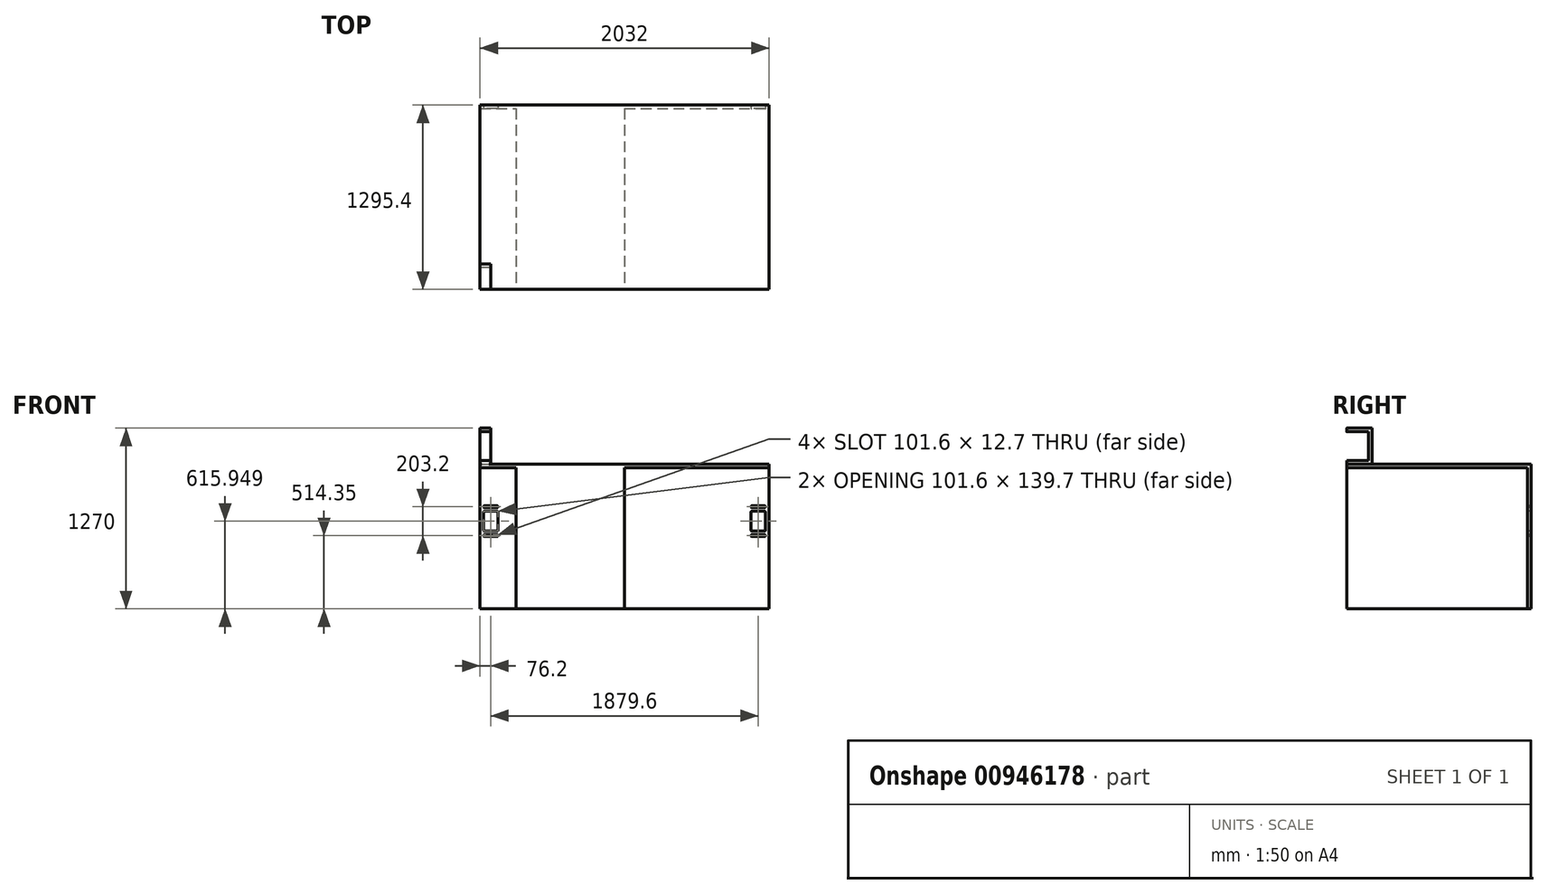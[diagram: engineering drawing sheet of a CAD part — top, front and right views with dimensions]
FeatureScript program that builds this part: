
annotation { "Feature Type Name" : "Feature", "Feature Type Description" : "" }
export const myFeature = defineFeature(function(context is Context, id is Id, definition is map)
    precondition{}
    {
        {
            var Q0;
            Q0=qCreatedBy(makeId("Front.planeOp"),FACE);
            var sketch = newSketch(context, id + "F0", { "sketchPlane" : qUnion([Q0])});
            skLineSegment(sketch, "E0.bottom", {"start": v(-762, 1162) * mm, "end": v(0, 1162) * mm});
            skLineSegment(sketch, "E0.top", {"start": v(-762, 146) * mm, "end": v(0, 146) * mm});
            skLineSegment(sketch, "E0.left", {"start": v(-762, 1162) * mm, "end": v(-762, 146) * mm});
            skLineSegment(sketch, "E0.right", {"start": v(0, 1162) * mm, "end": v(0, 146) * mm});
            skSolve(sketch);
        }
        {
            var Q0;
            Q0=qSketchRegion(id+"F0",true);
            extrude(context, id + "F1", {"entities" : qUnion([Q0]), "depth" : 1270 * mm, "offsetDistance" : 25.4 * mm});
        }
        {
            var Q0;
            Q0=makeQuery(id+"F1.opExtrude","CAP_FACE",FACE,{"disambiguationData":[OSD([sQuery(id+"F0.wireOp",EDGE,"E0.bottom"),sQuery(id+"F0.wireOp",EDGE,"E0.top"),sQuery(id+"F0.wireOp",EDGE,"E0.left"),sQuery(id+"F0.wireOp",EDGE,"E0.right")])],"isStart":true});
            var sketch = newSketch(context, id + "F2", { "sketchPlane" : qUnion([Q0])});
            skLineSegment(sketch, "E1.bottom", {"start": v(1016, 1162) * mm, "end": v(-1016, 1162) * mm});
            skLineSegment(sketch, "E1.top", {"start": v(1016, 146) * mm, "end": v(-1016, 146) * mm});
            skLineSegment(sketch, "E1.left", {"start": v(1016, 1162) * mm, "end": v(1016, 146) * mm});
            skLineSegment(sketch, "E1.right", {"start": v(-1016, 1162) * mm, "end": v(-1016, 146) * mm});
            skSolve(sketch);
        }
        {
            var Q0;
            Q0=qSketchRegion(id+"F2",true);
            extrude(context, id + "F3", {"entities" : qUnion([Q0]), "operationType" : NewBodyOperationType.ADD, "depth" : 25.4 * mm, "offsetDistance" : 25.4 * mm});
        }
        {
            var Q0;
            {var subQ0=sQuery(id+"F2.wireOp",EDGE,"E1.top");var subQ1=sQuery(id+"F2.wireOp",EDGE,"E1.bottom");var subQ2=sQuery(id+"F2.wireOp",EDGE,"E1.left");Q0=makeQuery(id+"F3.boolean.opBoolean","SPLIT",FACE,{"disambiguationData":[TD([makeQuery(id+"F1.opExtrude","SWEPT_FACE",FACE,{"disambiguationData":[OSD([sQuery(id+"F0.wireOp",EDGE,"E0.left")])]})])],"derivedFrom":makeQuery(id+"F3.opExtrude","CAP_FACE",FACE,{"disambiguationData":[OSD([subQ1,subQ0,subQ2,sQuery(id+"F2.wireOp",EDGE,"E1.right")])],"isStart":true})});}
            var sketch = newSketch(context, id + "F4", { "sketchPlane" : qUnion([Q0])});
            skLineSegment(sketch, "E2.bottom", {"start": v(990.6, 825.45) * mm, "end": v(990.6, 698.45) * mm});
            skLineSegment(sketch, "E2.top", {"start": v(889, 825.45) * mm, "end": v(889, 698.45) * mm});
            skLineSegment(sketch, "E2.left", {"start": v(984.25, 831.8) * mm, "end": v(895.35, 831.8) * mm});
            skLineSegment(sketch, "E2.right", {"start": v(984.25, 692.1) * mm, "end": v(895.35, 692.1) * mm});
            skLineSegment(sketch, "E3.bottom", {"start": v(990.6, 863.55) * mm, "end": v(990.6, 863.55) * mm});
            skLineSegment(sketch, "E3.top", {"start": v(889, 863.55) * mm, "end": v(889, 863.55) * mm});
            skLineSegment(sketch, "E3.left", {"start": v(984.25, 869.9) * mm, "end": v(895.35, 869.9) * mm});
            skLineSegment(sketch, "E3.right", {"start": v(984.25, 857.2) * mm, "end": v(895.35, 857.2) * mm});
            skLineSegment(sketch, "E4.bottom", {"start": v(990.6, 660.35) * mm, "end": v(990.6, 660.35) * mm});
            skLineSegment(sketch, "E4.top", {"start": v(889, 660.35) * mm, "end": v(889, 660.35) * mm});
            skLineSegment(sketch, "E4.left", {"start": v(984.25, 666.7) * mm, "end": v(895.35, 666.7) * mm});
            skLineSegment(sketch, "E4.right", {"start": v(984.25, 654) * mm, "end": v(895.35, 654) * mm});
            skPoint(sketch, "E5.visualSharp", {"position": v(990.6, 869.9) * mm});
            skArc(sketch, "E5.filletArc", {"start": v(990.6, 863.55) * mm, "mid": v(988.74, 868.04) * mm, "end": v(984.25, 869.9) * mm});
            skPoint(sketch, "E6.visualSharp", {"position": v(889, 857.2) * mm});
            skArc(sketch, "E6.filletArc", {"start": v(889, 863.55) * mm, "mid": v(890.86, 859.06) * mm, "end": v(895.35, 857.2) * mm});
            skPoint(sketch, "E7.visualSharp", {"position": v(889, 869.9) * mm});
            skArc(sketch, "E7.filletArc", {"start": v(895.35, 869.9) * mm, "mid": v(890.86, 868.04) * mm, "end": v(889, 863.55) * mm});
            skPoint(sketch, "E8.visualSharp", {"position": v(990.6, 857.2) * mm});
            skArc(sketch, "E8.filletArc", {"start": v(984.25, 857.2) * mm, "mid": v(988.74, 859.06) * mm, "end": v(990.6, 863.55) * mm});
            skPoint(sketch, "E9.visualSharp", {"position": v(990.6, 831.8) * mm});
            skArc(sketch, "E9.filletArc", {"start": v(990.6, 825.45) * mm, "mid": v(988.74, 829.94) * mm, "end": v(984.25, 831.8) * mm});
            skPoint(sketch, "E10.visualSharp", {"position": v(889, 831.8) * mm});
            skArc(sketch, "E10.filletArc", {"start": v(895.35, 831.8) * mm, "mid": v(890.86, 829.94) * mm, "end": v(889, 825.45) * mm});
            skPoint(sketch, "E11.visualSharp", {"position": v(990.6, 692.1) * mm});
            skArc(sketch, "E11.filletArc", {"start": v(984.25, 692.1) * mm, "mid": v(988.74, 693.96) * mm, "end": v(990.6, 698.45) * mm});
            skPoint(sketch, "E12.visualSharp", {"position": v(889, 692.1) * mm});
            skArc(sketch, "E12.filletArc", {"start": v(889, 698.45) * mm, "mid": v(890.86, 693.96) * mm, "end": v(895.35, 692.1) * mm});
            skPoint(sketch, "E13.visualSharp", {"position": v(990.6, 666.7) * mm});
            skArc(sketch, "E13.filletArc", {"start": v(990.6, 660.35) * mm, "mid": v(988.74, 664.84) * mm, "end": v(984.25, 666.7) * mm});
            skPoint(sketch, "E14.visualSharp", {"position": v(889, 654) * mm});
            skArc(sketch, "E14.filletArc", {"start": v(889, 660.35) * mm, "mid": v(890.86, 655.86) * mm, "end": v(895.35, 654) * mm});
            skPoint(sketch, "E15.visualSharp", {"position": v(889, 666.7) * mm});
            skArc(sketch, "E15.filletArc", {"start": v(895.35, 666.7) * mm, "mid": v(890.86, 664.84) * mm, "end": v(889, 660.35) * mm});
            skPoint(sketch, "E16.visualSharp", {"position": v(990.6, 654) * mm});
            skArc(sketch, "E16.filletArc", {"start": v(984.25, 654) * mm, "mid": v(988.74, 655.86) * mm, "end": v(990.6, 660.35) * mm});
            skLineSegment(sketch, "E17.bottom", {"start": v(-889, 825.45) * mm, "end": v(-889, 698.45) * mm});
            skLineSegment(sketch, "E17.top", {"start": v(-990.6, 825.45) * mm, "end": v(-990.6, 698.45) * mm});
            skLineSegment(sketch, "E17.left", {"start": v(-895.35, 831.8) * mm, "end": v(-984.25, 831.8) * mm});
            skLineSegment(sketch, "E17.right", {"start": v(-895.35, 692.1) * mm, "end": v(-984.25, 692.1) * mm});
            skLineSegment(sketch, "E18.bottom", {"start": v(-889, 863.55) * mm, "end": v(-889, 863.55) * mm});
            skLineSegment(sketch, "E18.top", {"start": v(-990.6, 863.55) * mm, "end": v(-990.6, 863.55) * mm});
            skLineSegment(sketch, "E18.left", {"start": v(-895.35, 869.9) * mm, "end": v(-984.25, 869.9) * mm});
            skLineSegment(sketch, "E18.right", {"start": v(-895.35, 857.2) * mm, "end": v(-984.25, 857.2) * mm});
            skLineSegment(sketch, "E19.bottom", {"start": v(-889, 660.35) * mm, "end": v(-889, 660.35) * mm});
            skLineSegment(sketch, "E19.top", {"start": v(-990.6, 660.35) * mm, "end": v(-990.6, 660.35) * mm});
            skLineSegment(sketch, "E19.left", {"start": v(-895.35, 666.7) * mm, "end": v(-984.25, 666.7) * mm});
            skLineSegment(sketch, "E19.right", {"start": v(-895.35, 654) * mm, "end": v(-984.25, 654) * mm});
            skPoint(sketch, "E20.visualSharp", {"position": v(-889, 869.9) * mm});
            skArc(sketch, "E20.filletArc", {"start": v(-889, 863.55) * mm, "mid": v(-890.86, 868.04) * mm, "end": v(-895.35, 869.9) * mm});
            skPoint(sketch, "E21.visualSharp", {"position": v(-990.6, 857.2) * mm});
            skArc(sketch, "E21.filletArc", {"start": v(-990.6, 863.55) * mm, "mid": v(-988.74, 859.06) * mm, "end": v(-984.25, 857.2) * mm});
            skPoint(sketch, "E22.visualSharp", {"position": v(-990.6, 869.9) * mm});
            skArc(sketch, "E22.filletArc", {"start": v(-984.25, 869.9) * mm, "mid": v(-988.74, 868.04) * mm, "end": v(-990.6, 863.55) * mm});
            skPoint(sketch, "E23.visualSharp", {"position": v(-889, 857.2) * mm});
            skArc(sketch, "E23.filletArc", {"start": v(-895.35, 857.2) * mm, "mid": v(-890.86, 859.06) * mm, "end": v(-889, 863.55) * mm});
            skPoint(sketch, "E24.visualSharp", {"position": v(-889, 831.8) * mm});
            skArc(sketch, "E24.filletArc", {"start": v(-889, 825.45) * mm, "mid": v(-890.86, 829.94) * mm, "end": v(-895.35, 831.8) * mm});
            skPoint(sketch, "E25.visualSharp", {"position": v(-990.6, 831.8) * mm});
            skArc(sketch, "E25.filletArc", {"start": v(-984.25, 831.8) * mm, "mid": v(-988.74, 829.94) * mm, "end": v(-990.6, 825.45) * mm});
            skPoint(sketch, "E26.visualSharp", {"position": v(-889, 692.1) * mm});
            skArc(sketch, "E26.filletArc", {"start": v(-895.35, 692.1) * mm, "mid": v(-890.86, 693.96) * mm, "end": v(-889, 698.45) * mm});
            skPoint(sketch, "E27.visualSharp", {"position": v(-990.6, 692.1) * mm});
            skArc(sketch, "E27.filletArc", {"start": v(-990.6, 698.45) * mm, "mid": v(-988.74, 693.96) * mm, "end": v(-984.25, 692.1) * mm});
            skPoint(sketch, "E28.visualSharp", {"position": v(-889, 666.7) * mm});
            skArc(sketch, "E28.filletArc", {"start": v(-889, 660.35) * mm, "mid": v(-890.86, 664.84) * mm, "end": v(-895.35, 666.7) * mm});
            skPoint(sketch, "E29.visualSharp", {"position": v(-990.6, 654) * mm});
            skArc(sketch, "E29.filletArc", {"start": v(-990.6, 660.35) * mm, "mid": v(-988.74, 655.86) * mm, "end": v(-984.25, 654) * mm});
            skPoint(sketch, "E30.visualSharp", {"position": v(-990.6, 666.7) * mm});
            skArc(sketch, "E30.filletArc", {"start": v(-984.25, 666.7) * mm, "mid": v(-988.74, 664.84) * mm, "end": v(-990.6, 660.35) * mm});
            skPoint(sketch, "E31.visualSharp", {"position": v(-889, 654) * mm});
            skArc(sketch, "E31.filletArc", {"start": v(-895.35, 654) * mm, "mid": v(-890.86, 655.86) * mm, "end": v(-889, 660.35) * mm});
            skSolve(sketch);
        }
        {
            var Q0;
            Q0=qSketchRegion(id+"F4",true);
            extrude(context, id + "F5", {"entities" : qUnion([Q0]), "operationType" : NewBodyOperationType.REMOVE, "oppositeDirection" : true, "depth" : 25.4 * mm, "offsetDistance" : 25.4 * mm});
        }
        {
            var Q0;
            Q0=makeQuery(id+"F3.boolean.opBoolean","MERGE",FACE,{"derivedFrom":[makeQuery(id+"F1.opExtrude","SWEPT_FACE",FACE,{"disambiguationData":[OSD([sQuery(id+"F0.wireOp",EDGE,"E0.bottom")])]}),makeQuery(id+"F3.opExtrude","SWEPT_FACE",FACE,{"disambiguationData":[OSD([sQuery(id+"F2.wireOp",EDGE,"E1.bottom")])]})]});
            var sketch = newSketch(context, id + "F6", { "sketchPlane" : qUnion([Q0])});
            skLineSegment(sketch, "E32.bottom", {"start": v(-1016, 0) * mm, "end": v(1016, 0) * mm});
            skLineSegment(sketch, "E32.top", {"start": v(-1016, -1270) * mm, "end": v(1016, -1270) * mm});
            skLineSegment(sketch, "E32.left", {"start": v(-1016, 0) * mm, "end": v(-1016, -1270) * mm});
            skLineSegment(sketch, "E32.right", {"start": v(1016, 0) * mm, "end": v(1016, -1270) * mm});
            skSolve(sketch);
        }
        {
            var Q0;
            Q0=qSketchRegion(id+"F6",true);
            extrude(context, id + "F7", {"entities" : qUnion([Q0]), "operationType" : NewBodyOperationType.ADD, "depth" : 0 * mm, "offsetDistance" : 25.4 * mm, "hasSecondDirection" : true, "secondDirectionOppositeDirection" : true, "secondDirectionDepth" : 25.4 * mm});
        }
        {
            var Q0;
            Q0=makeQuery(id+"F7.boolean.opBoolean","MERGE",FACE,{"derivedFrom":[makeQuery(id+"F3.boolean.opBoolean","MERGE",FACE,{"derivedFrom":[makeQuery(id+"F1.opExtrude","SWEPT_FACE",FACE,{"disambiguationData":[OSD([sQuery(id+"F0.wireOp",EDGE,"E0.bottom")])]}),makeQuery(id+"F3.opExtrude","SWEPT_FACE",FACE,{"disambiguationData":[OSD([sQuery(id+"F2.wireOp",EDGE,"E1.bottom")])]})]}),makeQuery(id+"F7.opExtrude","CAP_FACE",FACE,{"disambiguationData":[OSD([sQuery(id+"F6.wireOp",EDGE,"E32.bottom"),sQuery(id+"F6.wireOp",EDGE,"E32.top"),sQuery(id+"F6.wireOp",EDGE,"E32.left"),sQuery(id+"F6.wireOp",EDGE,"E32.right")])],"isStart":false})]});
            var sketch = newSketch(context, id + "F8", { "sketchPlane" : qUnion([Q0])});
            skLineSegment(sketch, "E33.bottom", {"start": v(-1003.3, -1270) * mm, "end": v(-952.5, -1270) * mm});
            skLineSegment(sketch, "E33.top", {"start": v(-1016, -1092.2) * mm, "end": v(-939.8, -1092.2) * mm});
            skLineSegment(sketch, "E33.left", {"start": v(-1016, -1257.3) * mm, "end": v(-1016, -1092.2) * mm});
            skLineSegment(sketch, "E33.right", {"start": v(-939.8, -1257.3) * mm, "end": v(-939.8, -1092.2) * mm});
            skPoint(sketch, "E34.visualSharp", {"position": v(-1016, -1270) * mm});
            skArc(sketch, "E34.filletArc", {"start": v(-1016, -1257.3) * mm, "mid": v(-1012.28, -1266.28) * mm, "end": v(-1003.3, -1270) * mm});
            skPoint(sketch, "E35.visualSharp", {"position": v(-939.8, -1270) * mm});
            skArc(sketch, "E35.filletArc", {"start": v(-952.5, -1270) * mm, "mid": v(-943.52, -1266.28) * mm, "end": v(-939.8, -1257.3) * mm});
            skSolve(sketch);
        }
        {
            var Q0;
            Q0=qSketchRegion(id+"F8",true);
            extrude(context, id + "F9", {"entities" : qUnion([Q0]), "operationType" : NewBodyOperationType.ADD, "depth" : 254 * mm, "offsetDistance" : 25.4 * mm});
        }
        {
            var Q0;
            Q0=makeQuery(id+"F9.boolean.opBoolean","MERGE",FACE,{"derivedFrom":[makeQuery(id+"F7.boolean.opBoolean","MERGE",FACE,{"derivedFrom":[makeQuery(id+"F3.opExtrude","SWEPT_FACE",FACE,{"disambiguationData":[OSD([sQuery(id+"F2.wireOp",EDGE,"E1.left")])]}),makeQuery(id+"F7.opExtrude","SWEPT_FACE",FACE,{"disambiguationData":[OSD([sQuery(id+"F6.wireOp",EDGE,"E32.left")])]})]}),makeQuery(id+"F9.opExtrude","SWEPT_FACE",FACE,{"disambiguationData":[OSD([sQuery(id+"F8.wireOp",EDGE,"E33.left")])]})]});
            var sketch = newSketch(context, id + "F10", { "sketchPlane" : qUnion([Q0])});
            skLineSegment(sketch, "E36.bottom", {"start": v(1117.6, 1187.4) * mm, "end": v(1270, 1187.4) * mm});
            skLineSegment(sketch, "E36.top", {"start": v(1117.6, 1390.6) * mm, "end": v(1270, 1390.6) * mm});
            skLineSegment(sketch, "E36.left", {"start": v(1117.6, 1187.4) * mm, "end": v(1117.6, 1390.6) * mm});
            skLineSegment(sketch, "E36.right", {"start": v(1270, 1187.4) * mm, "end": v(1270, 1390.6) * mm});
            skSolve(sketch);
        }
        {
            var Q0;
            Q0=qSketchRegion(id+"F10",true);
            extrude(context, id + "F11", {"entities" : qUnion([Q0]), "operationType" : NewBodyOperationType.REMOVE, "oppositeDirection" : true, "depth" : 76.2 * mm, "offsetDistance" : 25.4 * mm});
        }
    });
